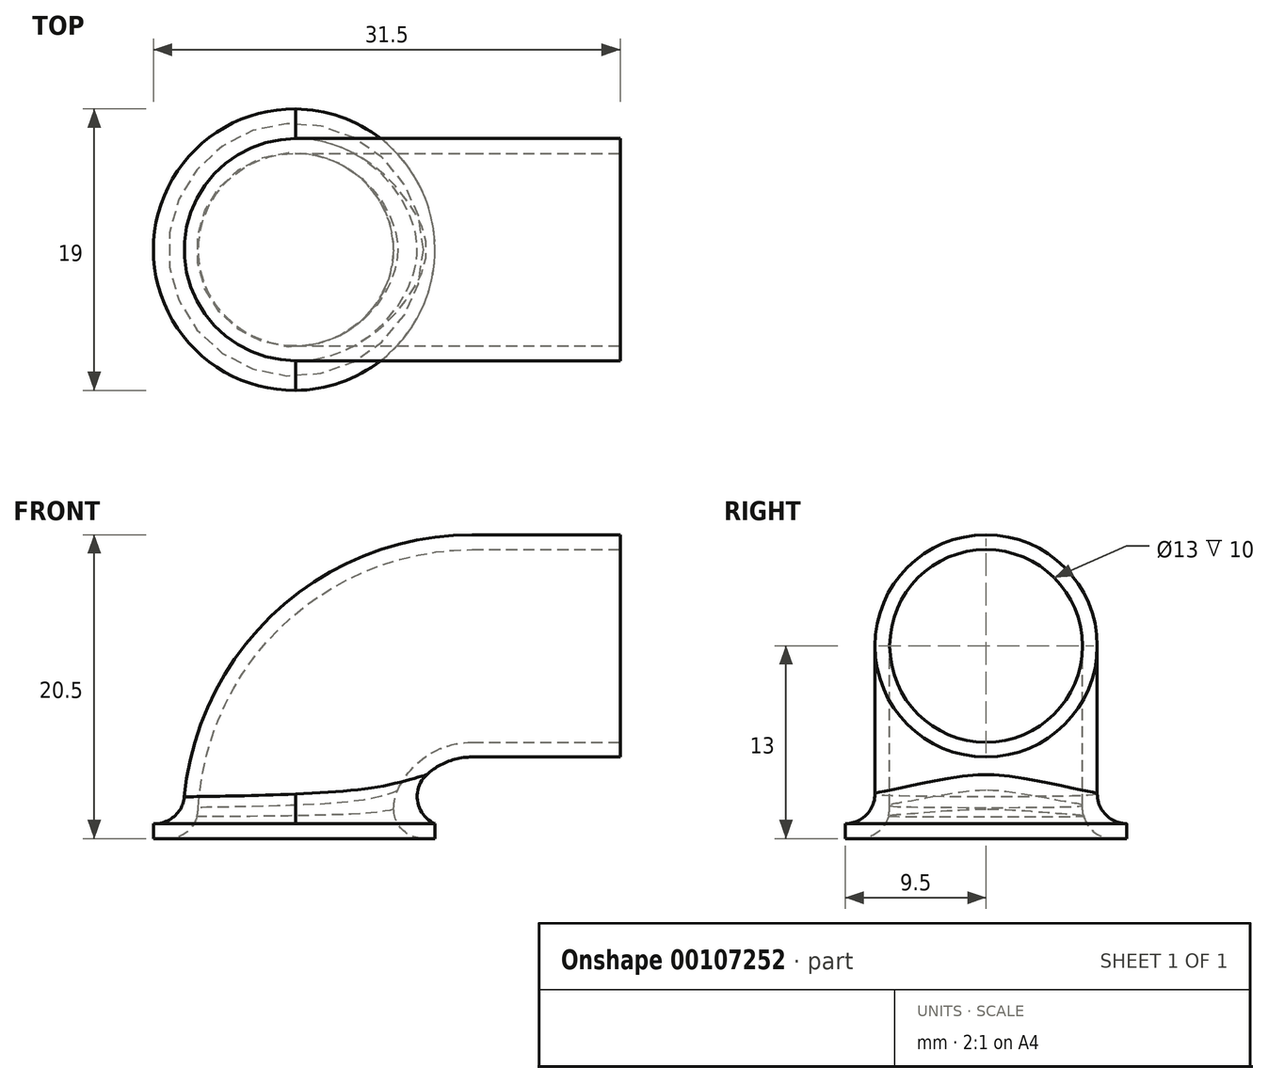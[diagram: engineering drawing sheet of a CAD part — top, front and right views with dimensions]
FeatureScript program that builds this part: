
annotation { "Feature Type Name" : "Feature", "Feature Type Description" : "" }
export const myFeature = defineFeature(function(context is Context, id is Id, definition is map)
    precondition{}
    {
        {
            var Q0;
            Q0=qCreatedBy(makeId("Top.planeOp"),FACE);
            var sketch = newSketch(context, id + "F0", { "sketchPlane" : qUnion([Q0])});
            skCircle(sketch, "E0", {"center": v(0, 0) * mm, "radius": 7.5 * mm});
            skCircle(sketch, "E1", {"center": v(0, 0) * mm, "radius": 6.5 * mm});
            skCircle(sketch, "E2", {"center": v(0, 0) * mm, "radius": 9.5 * mm});
            skSolve(sketch);
        }
        {
            var Q0;
            Q0=qCreatedBy(makeId("Front.planeOp"),FACE);
            var sketch = newSketch(context, id + "F1", { "sketchPlane" : qUnion([Q0])});
            skLineSegment(sketch, "E3", {"start": v(12, 13) * mm, "end": v(22, 13) * mm});
            skLineSegment(sketch, "E4", {"start": v(0, 0) * mm, "end": v(0, 1) * mm});
            skArc(sketch, "E5", {"start": v(0, 1) * mm, "mid": v(3.51, 9.49) * mm, "end": v(12, 13) * mm});
            skSolve(sketch);
        }
        {
            var Q0;
            Q0=makeQuery(id+"F0.imprint","IMPRINT",FACE,{"disambiguationData":[TD([[makeQuery(id+"F0.imprint","IMPRINT",EDGE,{"derivedFrom":sQuery(id+"F0.wireOp",EDGE,"E0")}),1.0]])]});
            var Q1;
            Q1=sQuery(id+"F0.wireOp",EDGE,"E0");
            var Q2;
            Q2=sQuery(id+"F1.wireOp",EDGE,"E4");
            var Q3;
            Q3=sQuery(id+"F1.wireOp",EDGE,"E5");
            var Q4;
            Q4=sQuery(id+"F1.wireOp",EDGE,"E3");
            sweep(context, id + "F2", {"profiles" : qUnion([Q0]), "surfaceProfiles" : qUnion([Q1]), "path" : qUnion([Q2, Q3, Q4])});
        }
        {
            var Q0;
            Q0=makeQuery(id+"F2.opSweep","CAP_EDGE",EDGE,{"disambiguationData":[OSD([sQuery(id+"F0.wireOp",EDGE,"E1"),sQuery(id+"F1.wireOp",VERTEX,"E4.start")])],"isStart":true});
            fillet(context, id + "F3", {"entities" : qUnion([Q0]), "radius" : 3 * mm, "tangentPropagation" : true, "allowEdgeOverflow" : false});
        }
        {
            var Q0;
            Q0 = qSketchRegion(id + "F0", true);
            extrude(context, id + "F4", {"entities" : qUnion([Q0]), "operationType" : NewBodyOperationType.ADD, "depth" : 1 * mm});
        }
        {
            var Q0;
            {var subQ0=sQuery(id+"F0.wireOp",EDGE,"E0");Q0=makeQuery(id+"F4.boolean.opBoolean","MERGE",EDGE,{"derivedFrom":[makeQuery(id+"F2.opSweep","MID_CAP_EDGE",EDGE,{"disambiguationData":[OSD([subQ0,sQuery(id+"F1.wireOp",VERTEX,"E5.start")])],"capPos":1.0}),makeQuery(id+"F4.opExtrude","CAP_EDGE",EDGE,{"disambiguationData":[OSD([subQ0])],"isStart":false})]});}
            fillet(context, id + "F5", {"entities" : qUnion([Q0]), "radius" : 2 * mm, "tangentPropagation" : true, "allowEdgeOverflow" : false});
        }
        {
            var Q0;
            Q0=makeQuery(id+"F2.opSweep","SWEPT_FACE",FACE,{"disambiguationData":[OSD([sQuery(id+"F0.wireOp",EDGE,"E1"),sQuery(id+"F1.wireOp",EDGE,"E5")])]});
            var Q1;
            {var subQ0=sQuery(id+"F0.wireOp",EDGE,"E0");Q1=makeQuery(id+"F4.boolean.opBoolean","MERGE",EDGE,{"derivedFrom":[makeQuery(id+"F3.opFillet","BLEND_EDGE",EDGE,{"blendedFrom":[makeQuery(id+"F2.opSweep","CAP_EDGE",EDGE,{"disambiguationData":[OSD([sQuery(id+"F0.wireOp",EDGE,"E1"),sQuery(id+"F1.wireOp",VERTEX,"E4.start")])],"isStart":true}),makeQuery(id+"F2.opSweep","SWEPT_FACE",FACE,{"disambiguationData":[OSD([subQ0,sQuery(id+"F1.wireOp",EDGE,"E4")])]})],"blendedInto":[makeQuery(id+"F2.opSweep","SWEPT_FACE",FACE,{"disambiguationData":[OSD([subQ0,sQuery(id+"F1.wireOp",EDGE,"E4")])]})]}),makeQuery(id+"F4.opExtrude","CAP_EDGE",EDGE,{"disambiguationData":[OSD([subQ0])],"isStart":true})]});}
            fillet(context, id + "F6", {"entities" : qUnion([Q0, Q1]), "radius" : 2 * mm, "tangentPropagation" : true, "allowEdgeOverflow" : false});
        }
    });
